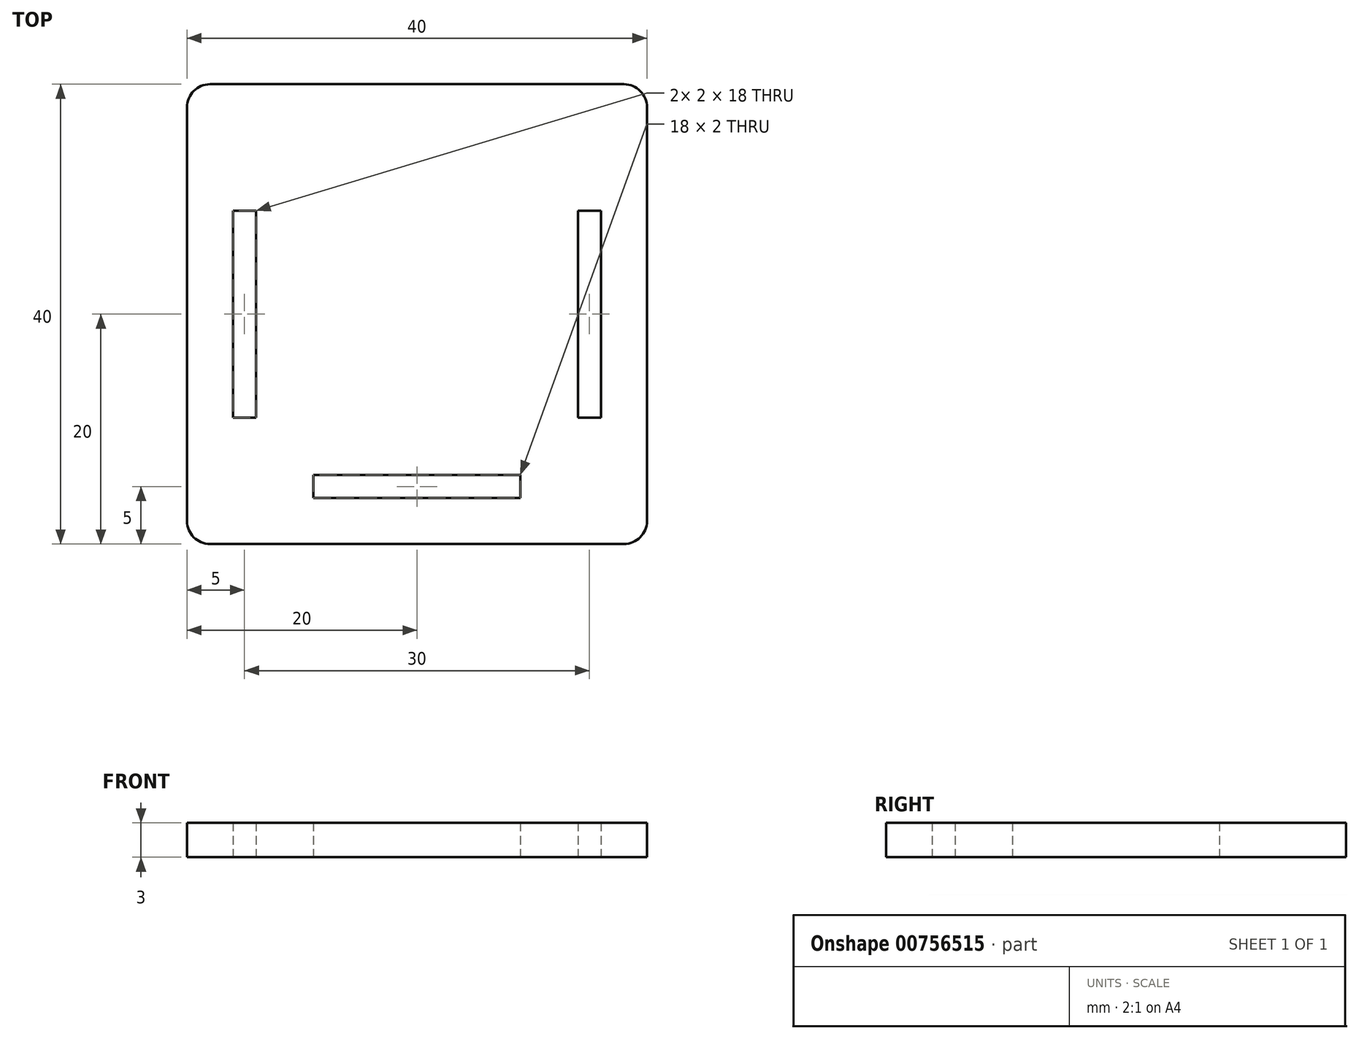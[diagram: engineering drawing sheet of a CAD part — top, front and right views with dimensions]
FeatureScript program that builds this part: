
annotation { "Feature Type Name" : "Feature", "Feature Type Description" : "" }
export const myFeature = defineFeature(function(context is Context, id is Id, definition is map)
    precondition{}
    {
        {
            var Q0;
            Q0=qCreatedBy(makeId("Top.planeOp"),FACE);
            var sketch = newSketch(context, id + "F0", { "sketchPlane" : qUnion([Q0])});
            skLineSegment(sketch, "E0.bottom", {"start": v(20, -20) * mm, "end": v(-20, -20) * mm});
            skLineSegment(sketch, "E0.top", {"start": v(20, 20) * mm, "end": v(-20, 20) * mm});
            skLineSegment(sketch, "E0.left", {"start": v(20, -20) * mm, "end": v(20, 20) * mm});
            skLineSegment(sketch, "E0.right", {"start": v(-20, -20) * mm, "end": v(-20, 20) * mm});
            skPoint(sketch, "E0.middle", {"position": v(0, 0) * mm});
            skLineSegment(sketch, "E1", {"start": v(0, 0) * mm, "end": v(0, -15) * mm, "construction": true});
            skLineSegment(sketch, "E2.bottom", {"start": v(9, -16) * mm, "end": v(-9, -16) * mm});
            skLineSegment(sketch, "E2.top", {"start": v(9, -14) * mm, "end": v(-9, -14) * mm});
            skLineSegment(sketch, "E2.left", {"start": v(9, -16) * mm, "end": v(9, -14) * mm});
            skLineSegment(sketch, "E2.right", {"start": v(-9, -16) * mm, "end": v(-9, -14) * mm});
            skPoint(sketch, "E2.middle", {"position": v(0, -15) * mm});
            skLineSegment(sketch, "E3", {"start": v(0, 0) * mm, "end": v(15, 0) * mm, "construction": true});
            skLineSegment(sketch, "E4", {"start": v(0, 0) * mm, "end": v(-15, 0) * mm, "construction": true});
            skLineSegment(sketch, "E5.bottom", {"start": v(-14, -9) * mm, "end": v(-16, -9) * mm});
            skLineSegment(sketch, "E5.top", {"start": v(-14, 9) * mm, "end": v(-16, 9) * mm});
            skLineSegment(sketch, "E5.left", {"start": v(-14, -9) * mm, "end": v(-14, 9) * mm});
            skLineSegment(sketch, "E5.right", {"start": v(-16, -9) * mm, "end": v(-16, 9) * mm});
            skPoint(sketch, "E5.middle", {"position": v(-15, 0) * mm});
            skLineSegment(sketch, "E6.bottom", {"start": v(16, -9) * mm, "end": v(14, -9) * mm});
            skLineSegment(sketch, "E6.top", {"start": v(16, 9) * mm, "end": v(14, 9) * mm});
            skLineSegment(sketch, "E6.left", {"start": v(16, -9) * mm, "end": v(16, 9) * mm});
            skLineSegment(sketch, "E6.right", {"start": v(14, -9) * mm, "end": v(14, 9) * mm});
            skPoint(sketch, "E6.middle", {"position": v(15, 0) * mm});
            skSolve(sketch);
        }
        {
            var Q0;
            Q0 = qSketchRegion(id + "F0", true);
            extrude(context, id + "F1", {"entities" : qUnion([Q0]), "depth" : 3 * mm, "offsetDistance" : 25 * mm});
        }
        {
            var Q0;
            Q0=makeQuery(id+"F1.opExtrude","SWEPT_EDGE",EDGE,{"disambiguationData":[OSD([sQuery(id+"F0.wireOp",EDGE,"E0.bottom"),sQuery(id+"F0.wireOp",EDGE,"E0.left")])]});
            var Q1;
            Q1=makeQuery(id+"F1.opExtrude","SWEPT_EDGE",EDGE,{"disambiguationData":[OSD([sQuery(id+"F0.wireOp",EDGE,"E0.bottom"),sQuery(id+"F0.wireOp",EDGE,"E0.right")])]});
            var Q2;
            Q2=makeQuery(id+"F1.opExtrude","SWEPT_EDGE",EDGE,{"disambiguationData":[OSD([sQuery(id+"F0.wireOp",EDGE,"E0.top"),sQuery(id+"F0.wireOp",EDGE,"E0.right")])]});
            var Q3;
            Q3=makeQuery(id+"F1.opExtrude","SWEPT_EDGE",EDGE,{"disambiguationData":[OSD([sQuery(id+"F0.wireOp",EDGE,"E0.top"),sQuery(id+"F0.wireOp",EDGE,"E0.left")])]});
            fillet(context, id + "F2", {"entities" : qUnion([Q0, Q1, Q2, Q3]), "radius" : 2 * mm, "tangentPropagation" : true, "allowEdgeOverflow" : false});
        }
    });
